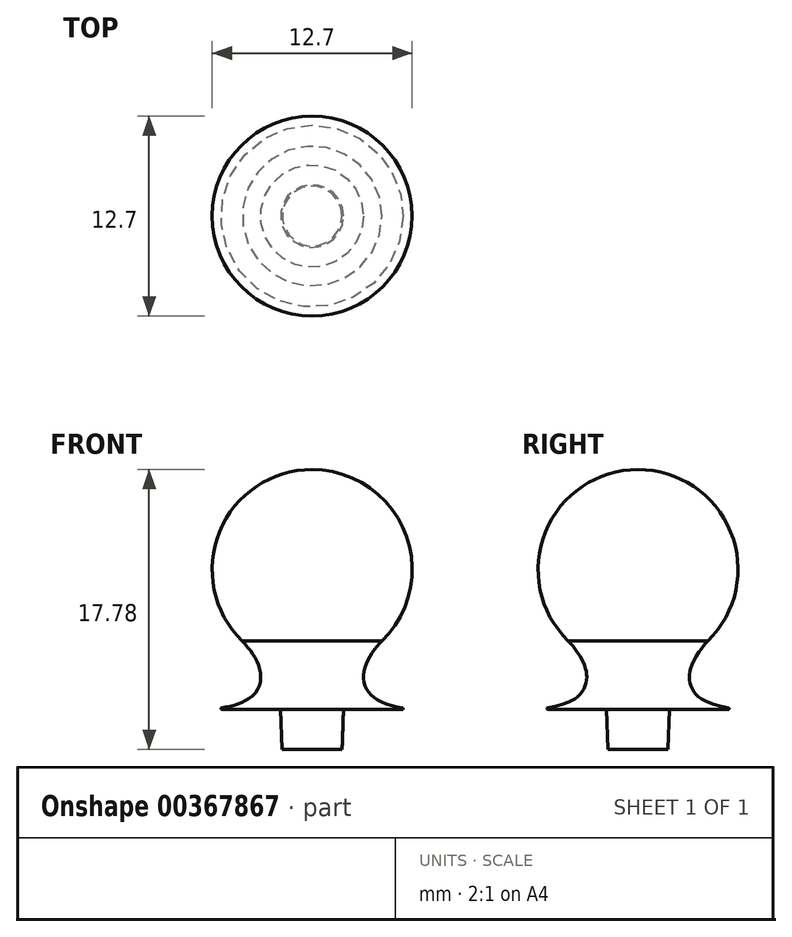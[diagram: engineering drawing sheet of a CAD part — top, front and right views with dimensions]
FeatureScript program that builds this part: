
annotation { "Feature Type Name" : "Feature", "Feature Type Description" : "" }
export const myFeature = defineFeature(function(context is Context, id is Id, definition is map)
    precondition{}
    {
        {
            var Q0;
            Q0=qCreatedBy(makeId("Front.planeOp"),FACE);
            var sketch = newSketch(context, id + "F0", { "sketchPlane" : qUnion([Q0])});
            skArc(sketch, "E0", {"start": v(-2.13, -1.99) * mm, "mid": v(4.22, 4.36) * mm, "end": v(-2.13, 10.71) * mm});
            skLineSegment(sketch, "E1.0", {"start": v(70.64, -4.53) * mm, "end": v(-74.9, -4.53) * mm});
            skFitSpline(sketch, "E2", {"points": [v(2.5, 0.02) * mm, v(1.31, -1.61) * mm, v(1.42, -3.4) * mm, v(5.09, -4.53) * mm], "startDerivative": vector(-3.53, -3.48) * mm, "endDerivative": vector(13.25, 0) * mm});
            skLineSegment(sketch, "E3", {"start": v(-2.13, 10.71) * mm, "end": v(-2.13, -4.53) * mm});
            skLineSegment(sketch, "E4.bottom", {"start": v(-2.13, -4.53) * mm, "end": v(-0.23, -4.53) * mm});
            skLineSegment(sketch, "E4.top", {"start": v(-2.13, -7.07) * mm, "end": v(-0.23, -7.07) * mm});
            skLineSegment(sketch, "E4.left", {"start": v(-2.13, -4.53) * mm, "end": v(-2.13, -7.07) * mm});
            skLineSegment(sketch, "E5", {"start": v(-0.23, -7.07) * mm, "end": v(-0.14, -4.53) * mm});
            skSolve(sketch);
        }
        {
            var Q0;
            Q0 = qSketchRegion(id + "F0", true);
            var Q1;
            Q1=sQuery(id+"F0.wireOp",EDGE,"E3");
            revolve(context, id + "F1", {"entities" : qUnion([Q0]), "axis" : qUnion([Q1]), "revolveType" : RevolveType.FULL});
        }
        {
            var Q0;
            Q0=makeQuery(id+"F1.opRevolve","SWEPT_EDGE",EDGE,{"disambiguationData":[OSD([sQuery(id+"F0.wireOp",EDGE,"E1.0"),sQuery(id+"F0.wireOp",EDGE,"E2")])]});
            fillet(context, id + "F2", {"entities" : qUnion([Q0]), "radius" : 0.05 * mm, "tangentPropagation" : true, "allowEdgeOverflow" : false});
        }
    });
